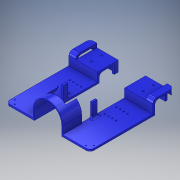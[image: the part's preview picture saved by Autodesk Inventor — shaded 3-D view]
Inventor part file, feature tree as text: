
AUTODESK INVENTOR PART (.ipt)
format: ipt  version: 2019 (Build 230136000, 136)  size: 452,096 bytes
history: native  units: in
note: dims shown in document units (in); Inventor stores cm internally (conversion verified against a paired STEP export)
features: extrude x17, sketch x16, fillet x2, mirror x1
ambient origin geometry x8: Origin, YZ Plane, XZ Plane, XY Plane, X Axis, Y Axis, Z Axis, Center Point
bodies: Solid1 (feature_tree)
feature tree (36):
  extrude  "Extrusion1"  Depth=1.422in
  extrude  "Extrusion2"  Depth=1.422in
  extrude  "Extrusion3"  Depth=0.1969in TaperAngle=0.0deg
  extrude  "Extrusion4"  Depth=0.1969in
  extrude  "Extrusion5"  Depth=2.25in
  extrude  "Extrusion6"  Depth=0.1969in TaperAngle=0.0deg
  extrude  "Extrusion7"  Depth=0.1969in
  extrude  "Extrusion8"  Depth=0.1969in
  extrude  "Extrusion9"  Depth=1.68in
  extrude  "Extrusion10"  Depth=0.5315in
  extrude  "Extrusion11"  Depth=0.1575in
  extrude  "Extrusion12"  Depth=1.0in TaperAngle=0.0deg
  extrude  "Extrusion13"  Depth=0.1969in
  mirror  "Mirror1"
  fillet  "Fillet4"  Radius=0.886in
  fillet  "Fillet5"  Radius=2.7638in
  extrude  "Extrusion14"  Depth=0.7874in
  sketch  "Sketch17"  dims[d39=1.6142in d40=1.5748in]
  extrude  "Extrusion15"  Depth=1.5748in
  extrude  "Extrusion16"  Depth=1.9685in
  extrude  "Extrusion17"  Depth=1.9685in
  sketch  "Sketch1"  dims[d0=1.422in d1=2.17in]
  sketch  "Sketch3"  dims[d2=1.422in d3=2.953in]
  sketch  "Sketch4"  dims[d4=6.75in d5=0.1969in d6=0.0in]
  sketch  "Sketch5"  dims[d7=2.953in d8=0.1969in]
  sketch  "Sketch6"  dims[d9=1.2992in d10=0.0in d11=2.25in]
  sketch  "Sketch8"  dims[d12=0.1969in d13=0.4134in d14=0.0in]
  sketch  "Sketch9"  dims[d15=0.1969in d16=0.1969in]
  sketch  "Sketch10"  dims[d17=2.0in d18=0.0in d19=0.1969in]
  sketch  "Sketch11"  dims[d20=0.4134in d21=0.0in d22=1.68in]
  sketch  "Sketch12"  dims[d23=0.9843in d24=0.5315in]
  sketch  "Sketch13"  dims[d25=1.063in d26=0.1575in]
  sketch  "Sketch14"  dims[d27=0.1575in d28=1.0in d29=0.0in]
  sketch  "Sketch15"  dims[d32=2.25in d33=0.1969in d34=0.886in d35=0.0in d36=2.7638in]
  sketch  "Sketch16"  dims[d37=4.0787in d38=0.7874in]
  sketch  "Sketch18"  dims[d41=0.2362in d42=0.6102in d43=0.1378in d44=0.2362in d45=0.6102in d46=0.1378in d47=1.5748in d49=0.3937in d50=0.3937in d52=1.0in d54=0.886in d55=0.0in d56=0.4528in d57=0.4528in d58=0.9055in d59=0.2953in d60=135.0deg d61=0.5906in d62=0.1181in d63=0.1181in d64=0.1969in d65=0.0in d66=0.1969in d67=5.25in d68=0.1969in d69=0.5in d70=1.45in d71=0.0in d72=0.25in d73=0.1969in d74=0.1575in d75=0.3937in d76=0.0in d77=0.1969in d78=0.2362in d79=0.0in d80=0.1181in d81=0.1575in d82=0.1575in d83=0.2362in d84=0.0in d88=0.3937in d89=0.1969in d90=2.1732in d91=0.1181in d92=1.9685in d93=1.9685in d94=0.1181in d95=1.9685in d96=0.0in d97=0.3937in d98=1.5401in d99=180.0deg d100=180.0deg d101=1.9685in d102=0.0in d103=180.0deg d104=1.9685in d105=0.0in d107=7.874in d108=90.0deg d109=0.9843in d110=180.0deg d111=1.9685in d112=2.7559in d113=0.0in]
